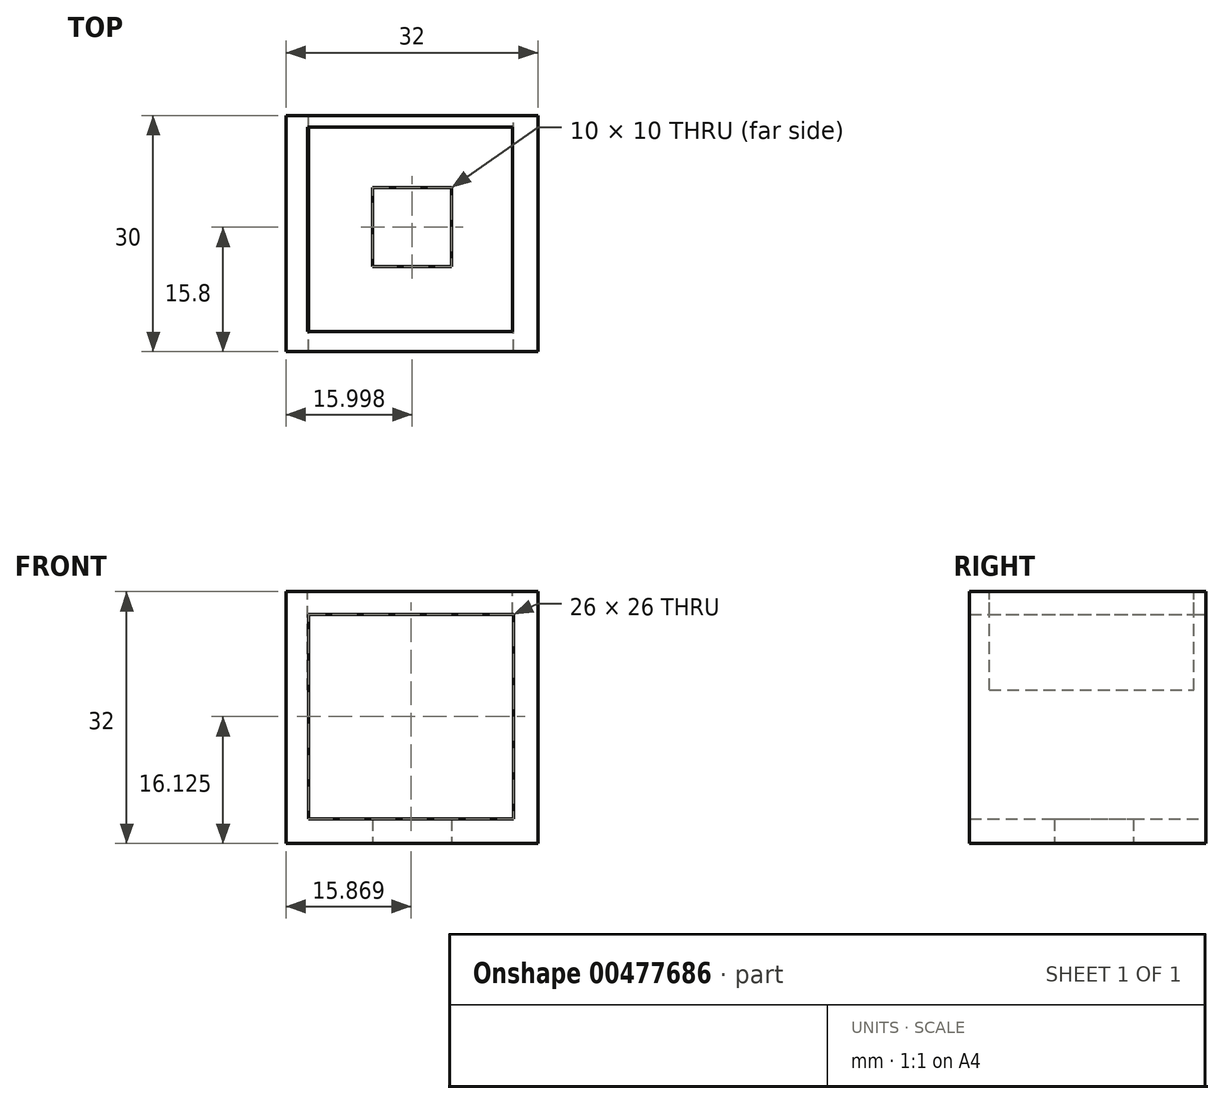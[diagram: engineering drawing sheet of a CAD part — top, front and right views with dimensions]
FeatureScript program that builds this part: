
annotation { "Feature Type Name" : "Feature", "Feature Type Description" : "" }
export const myFeature = defineFeature(function(context is Context, id is Id, definition is map)
    precondition{}
    {
        {
            var Q0;
            Q0=qCreatedBy(makeId("Front.planeOp"),FACE);
            var sketch = newSketch(context, id + "F0", { "sketchPlane" : qUnion([Q0])});
            skLineSegment(sketch, "E0.bottom", {"start": v(-16.18, 7.19) * mm, "end": v(-48.18, 7.19) * mm});
            skLineSegment(sketch, "E0.top", {"start": v(-16.18, 39.19) * mm, "end": v(-48.18, 39.19) * mm});
            skLineSegment(sketch, "E0.left", {"start": v(-16.18, 7.19) * mm, "end": v(-16.18, 39.19) * mm});
            skLineSegment(sketch, "E0.right", {"start": v(-48.18, 7.19) * mm, "end": v(-48.18, 39.19) * mm});
            skPoint(sketch, "E0.middle", {"position": v(-32.18, 23.19) * mm});
            skSolve(sketch);
        }
        {
            var Q0;
            Q0=makeQuery(id+"F0.imprint","IMPRINT",FACE,{"disambiguationData":[TD([[makeQuery(id+"F0.imprint","IMPRINT",EDGE,{"derivedFrom":sQuery(id+"F0.wireOp",EDGE,"E0.bottom")}),-1.0]])]});
            var Q1;
            Q1=qSketchRegion(id+"FY4OKqCvvIF9WiA_1",true);
            extrude(context, id + "F1", {"entities" : qUnion([Q0, Q1]), "depth" : 30 * mm});
        }
        {
            var Q0;
            Q0=qCreatedBy(makeId("Front.planeOp"),FACE);
            var sketch = newSketch(context, id + "F2", { "sketchPlane" : qUnion([Q0])});
            skLineSegment(sketch, "E1.bottom", {"start": v(-45.31, 10.32) * mm, "end": v(-19.31, 10.32) * mm});
            skLineSegment(sketch, "E1.top", {"start": v(-45.31, 36.32) * mm, "end": v(-19.31, 36.32) * mm});
            skLineSegment(sketch, "E1.left", {"start": v(-45.31, 10.32) * mm, "end": v(-45.31, 36.32) * mm});
            skLineSegment(sketch, "E1.right", {"start": v(-19.31, 10.32) * mm, "end": v(-19.31, 36.32) * mm});
            skPoint(sketch, "E1.middle", {"position": v(-32.31, 23.32) * mm});
            skSolve(sketch);
        }
        {
            var Q0;
            Q0=qSketchRegion(id+"F2",true);
            var Q1;
            Q1=qConstructionFilter(qBodyType(qCreatedBy(id+"F2",EDGE),BodyType.WIRE),ConstructionObject.NO);
            extrude(context, id + "F3", {"entities" : qUnion([Q0]), "operationType" : NewBodyOperationType.REMOVE, "surfaceEntities" : qUnion([Q1]), "endBound" : BoundingType.THROUGH_ALL, "depth" : 25 * mm});
        }
        {
            var Q0;
            Q0=makeQuery(id+"F1.opExtrude","SWEPT_FACE",FACE,{"disambiguationData":[OSD([sQuery(id+"F0.wireOp",EDGE,"E0.top")])]});
            var sketch = newSketch(context, id + "F4", { "sketchPlane" : qUnion([Q0])});
            skLineSegment(sketch, "E2.bottom", {"start": v(-45.44, -27.49) * mm, "end": v(-19.44, -27.49) * mm});
            skLineSegment(sketch, "E2.top", {"start": v(-45.44, -1.49) * mm, "end": v(-19.44, -1.49) * mm});
            skLineSegment(sketch, "E2.left", {"start": v(-45.44, -27.49) * mm, "end": v(-45.44, -1.49) * mm});
            skLineSegment(sketch, "E2.right", {"start": v(-19.44, -27.49) * mm, "end": v(-19.44, -1.49) * mm});
            skPoint(sketch, "E2.middle", {"position": v(-32.44, -14.49) * mm});
            skSolve(sketch);
        }
        {
            var Q0;
            Q0=qSketchRegion(id+"F4",true);
            extrude(context, id + "F5", {"entities" : qUnion([Q0]), "operationType" : NewBodyOperationType.REMOVE, "endBound" : BoundingType.SYMMETRIC, "oppositeDirection" : true, "depth" : 25 * mm});
        }
        {
            var Q0;
            Q0=makeQuery(id+"F1.opExtrude","SWEPT_FACE",FACE,{"disambiguationData":[OSD([sQuery(id+"F0.wireOp",EDGE,"E0.bottom")])]});
            var sketch = newSketch(context, id + "F6", { "sketchPlane" : qUnion([Q0])});
            skLineSegment(sketch, "E3.bottom", {"start": v(-37.18, 9.2) * mm, "end": v(-27.18, 9.2) * mm});
            skLineSegment(sketch, "E3.top", {"start": v(-37.18, 19.2) * mm, "end": v(-27.18, 19.2) * mm});
            skLineSegment(sketch, "E3.left", {"start": v(-37.18, 9.2) * mm, "end": v(-37.18, 19.2) * mm});
            skLineSegment(sketch, "E3.right", {"start": v(-27.18, 9.2) * mm, "end": v(-27.18, 19.2) * mm});
            skPoint(sketch, "E3.middle", {"position": v(-32.18, 14.2) * mm});
            skPoint(sketch, "E3.middle.positionSnap0", {"position": v(-32.18, 30) * mm});
            skPoint(sketch, "E3.centerSnap0", {"position": v(-32.18, 30) * mm});
            skSolve(sketch);
        }
        {
            var Q0;
            Q0=qSketchRegion(id+"F6",true);
            extrude(context, id + "F7", {"entities" : qUnion([Q0]), "operationType" : NewBodyOperationType.REMOVE, "endBound" : BoundingType.THROUGH_ALL, "oppositeDirection" : true, "depth" : 25 * mm});
        }
    });
